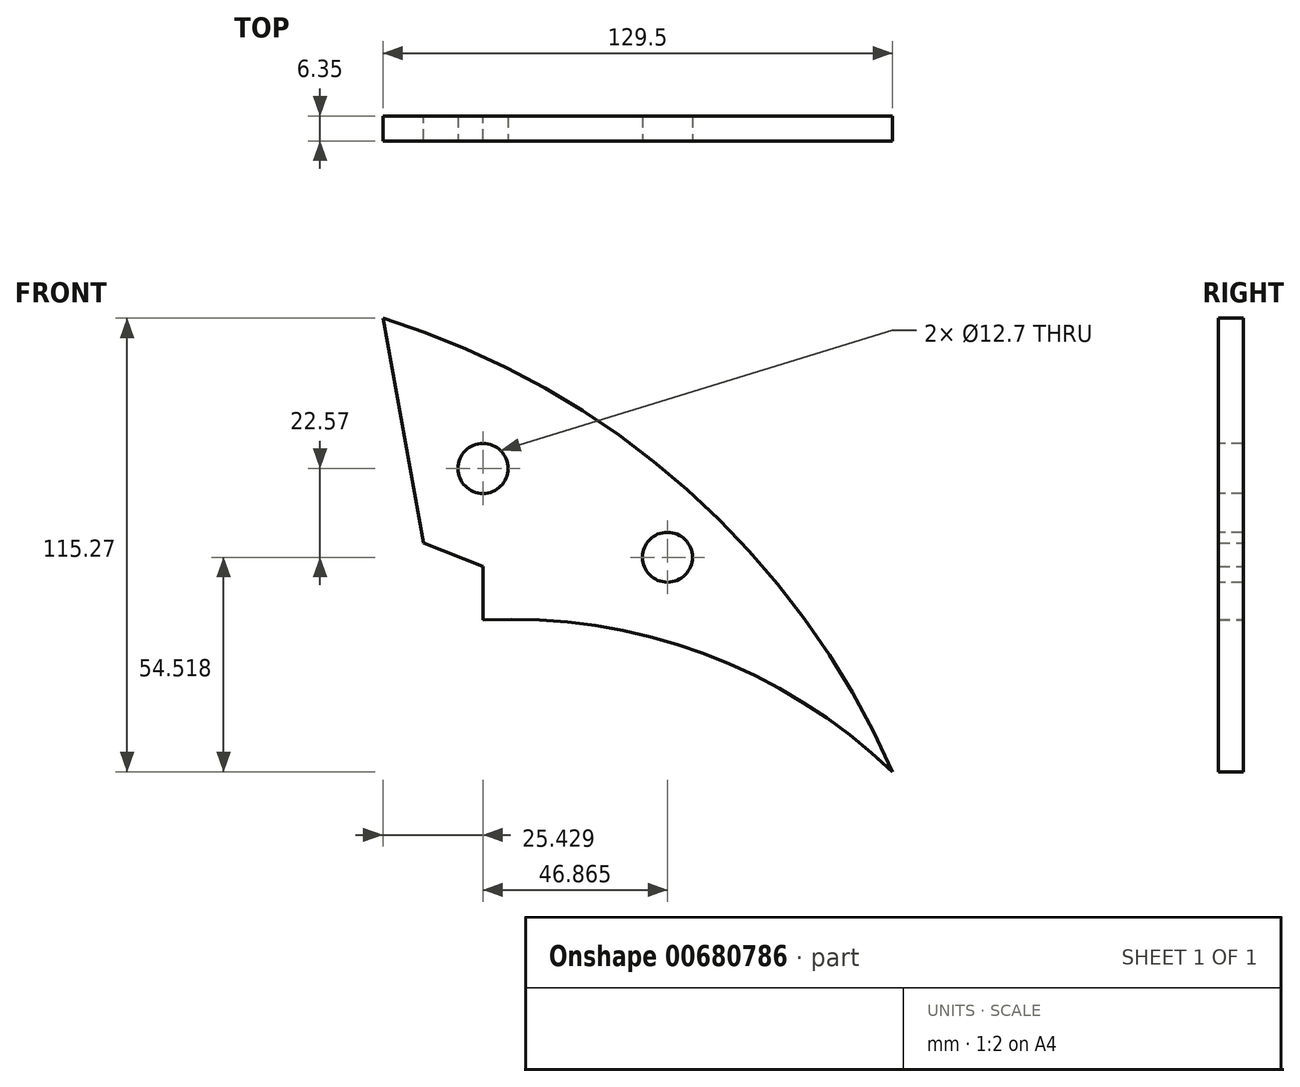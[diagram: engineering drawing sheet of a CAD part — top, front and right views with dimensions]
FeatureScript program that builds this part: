
annotation { "Feature Type Name" : "Feature", "Feature Type Description" : "" }
export const myFeature = defineFeature(function(context is Context, id is Id, definition is map)
    precondition{}
    {
        {
            var Q0;
            Q0=qCreatedBy(makeId("Front.planeOp"),FACE);
            var sketch = newSketch(context, id + "F0", { "sketchPlane" : qUnion([Q0])});
            skArc(sketch, "E0", {"start": v(59.27, 0) * mm, "mid": v(7.03, 71.69) * mm, "end": v(-70.23, 115.27) * mm});
            skArc(sketch, "E1", {"start": v(59.27, 0) * mm, "mid": v(11.22, 30.03) * mm, "end": v(-44.8, 38.53) * mm});
            skLineSegment(sketch, "E2", {"start": v(-44.8, 38.53) * mm, "end": v(-44.8, 52.13) * mm});
            skLineSegment(sketch, "E3", {"start": v(-44.8, 52.13) * mm, "end": v(-59.92, 58.08) * mm});
            skLineSegment(sketch, "E4", {"start": v(-59.92, 58.08) * mm, "end": v(-70.23, 115.27) * mm});
            skSolve(sketch);
        }
        {
            var Q0;
            Q0=makeQuery(id+"F0.imprint","IMPRINT",FACE,{"disambiguationData":[TD([[makeQuery(id+"F0.imprint","IMPRINT",EDGE,{"derivedFrom":sQuery(id+"F0.wireOp",EDGE,"E0")}),1.0]])]});
            extrude(context, id + "F1", {"entities" : qUnion([Q0]), "depth" : 6.35 * mm, "offsetDistance" : 25.4 * mm});
        }
        {
            var Q0;
            Q0=makeQuery(id+"F1.opExtrude","CAP_FACE",FACE,{"disambiguationData":[OSD([sQuery(id+"F0.wireOp",EDGE,"E0"),sQuery(id+"F0.wireOp",EDGE,"E1"),sQuery(id+"F0.wireOp",EDGE,"E2"),sQuery(id+"F0.wireOp",EDGE,"E3"),sQuery(id+"F0.wireOp",EDGE,"E4")])],"isStart":false});
            var sketch = newSketch(context, id + "F2", { "sketchPlane" : qUnion([Q0])});
            skCircle(sketch, "E5", {"center": v(-44.8, 77.09) * mm, "radius": 6.5 * mm});
            skCircle(sketch, "E6", {"center": v(2.06, 54.52) * mm, "radius": 6.57 * mm});
            skSolve(sketch);
        }
        {
            var Q0;
            Q0=sQuery(id+"F2.wireOp",VERTEX,"E5.center");
            var Q1;
            Q1=sQuery(id+"F2.wireOp",VERTEX,"E6.center");
            var Q2;
            Q2=makeQuery(id+"F1.opExtrude","SWEPT_BODY",BODY,{"disambiguationData":[OSD([sQuery(id+"F0.wireOp",EDGE,"E0"),sQuery(id+"F0.wireOp",EDGE,"E1"),sQuery(id+"F0.wireOp",EDGE,"E2"),sQuery(id+"F0.wireOp",EDGE,"E3"),sQuery(id+"F0.wireOp",EDGE,"E4")])]});
            hole(context, id + "F3", {"style" : HoleStyle.SIMPLE, "endStyle" : HoleEndStyle.THROUGH, "holeDiameter" : 12.7 * mm, "majorDiameter" : 6.35 * mm, "isTappedThrough" : true, "tappedDepth" : 12.7 * mm, "tapClearance" : 3, "locations" : qUnion([Q0, Q1]), "scope" : qUnion([Q2])});
        }
    });
